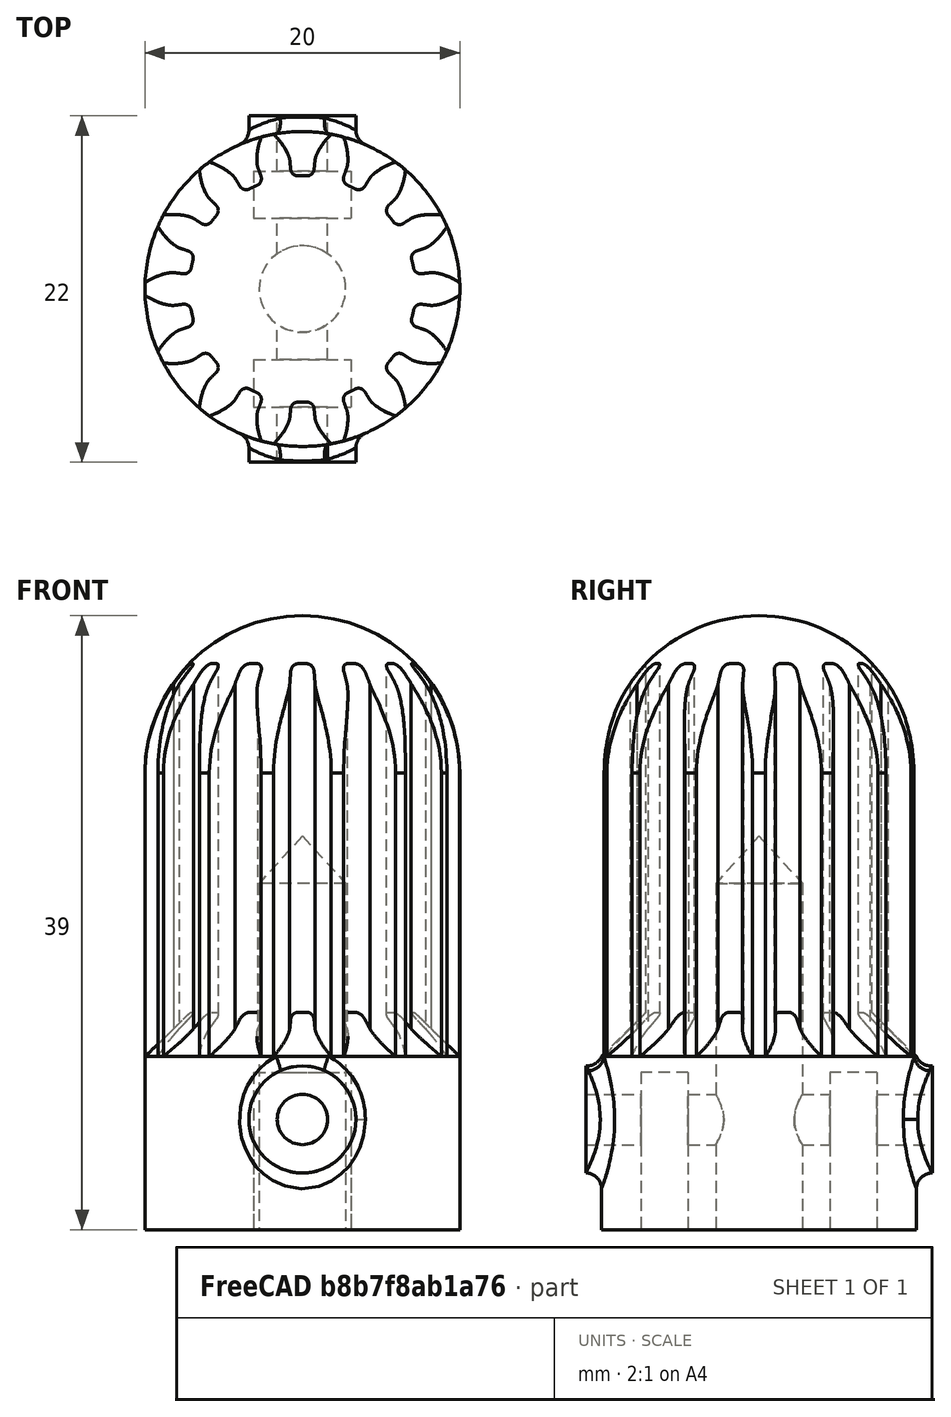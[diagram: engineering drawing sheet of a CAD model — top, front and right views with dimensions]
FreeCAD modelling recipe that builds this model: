
FCSTD DOCUMENT  (FreeCAD 0.14R3700 (Git))
Label: SmallGear
License: CC-BY 3.0
LicenseURL: http://creativecommons.org/licenses/by/3.0/
objects: Part::Cylinder×5, Part::Box×3, Part::Cut×3, Part::Sphere×2, Part::Cone×2, Part::MultiFuse×2, Part::Part2DObjectPython×1, PartDesign::Pad×1, Part::Fillet×1
note: 21 computed .brp shape members not serialized (recipe doc carries the construction recipe); baked Part::Feature solids carry a one-line shape summary decoded from their .brp

FEATURE [Part::Cylinder] Cylinder  label="CylinderBase"
  Angle = 360
  Height = 11
  Placement = pos=(0,0,28) rot=(0,0,1;0rad)
  Radius = 10
FEATURE [Part::Cylinder] Cylinder001  label="DeltaCylinderShaft"
  Angle = 360
  Height = 22
  Placement = pos=(0,0,17) rot=(0,0,1;0rad)
  Radius = 2.75
FEATURE [Part::Part2DObjectPython] InvoluteGear  # Draft 2D object (typed FeaturePython)
  Modules = 1.25
  NumberOfCurves = 0
  NumberOfTeeth = 14
  PressureAngle = 20
FEATURE [PartDesign::Pad] Pad
  Length = 28
  Length2 = 100
  Sketch = -> InvoluteGear
  Type = 0
FEATURE [Part::Box] Box  label="DeltaNutPocket1"
  Height = 10
  Length = 6.2
  Placement = pos=(-3.1,4.5,29) rot=(0,0,1;0rad)
  Width = 3
FEATURE [Part::Box] Box001  label="DeltaNutPocket2"
  Height = 10
  Length = 6.2
  Placement = pos=(-3.1,-7.5,29) rot=(0,0,1;0rad)
  Width = 3
FEATURE [Part::Cylinder] Cylinder002  label="DeltaCylinderM3"
  Angle = 360
  Height = 25
  Placement = pos=(0,13,32) rot=(1,0,0;1.5708rad)
  Radius = 1.6
FEATURE [Part::Sphere] Sphere  label="SphereTop"
  Angle1 = -90
  Angle2 = 90
  Angle3 = 360
  Placement = pos=(0,0,10) rot=(0,0,1;0rad)
  Radius = 10
FEATURE [Part::Box] Box002  label="DeltaCube"
  Height = 22
  Length = 44
  Placement = pos=(-22,-22,10) rot=(0,0,1;0rad)
  Width = 44
FEATURE [Part::Cone] Cone  label="ConeBase"
  Angle = 360
  Height = 5
  Placement = pos=(0,0,23) rot=(0,0,1;0rad)
  Radius1 = 5
  Radius2 = 10
FEATURE [Part::Sphere] Sphere001  label="SphereTopOutter"
  Angle1 = -90
  Angle2 = 90
  Angle3 = 360
  Placement = pos=(0,0,10) rot=(0,0,1;0rad)
  Radius = 20
FEATURE [Part::Cut] Cut
  Base = -> Sphere001
  Tool = -> Sphere
FEATURE [Part::Cut] Cut001  label="DeltaSphere"
  Base = -> Cut
  Tool = -> Box002
FEATURE [Part::Cone] Cone001  label="DeltaCylinderShaftTop"
  Angle = 360
  Height = 3
  Placement = pos=(0,0,14) rot=(0,0,1;0rad)
  Radius1 = 0
  Radius2 = 2.75
FEATURE [Part::Cylinder] Cylinder003  label="CylinderReenforcement1"
  Angle = 360
  Height = 3
  Placement = pos=(0,11,32) rot=(1,0,0;1.5708rad)
  Radius = 3.4
FEATURE [Part::Cylinder] Cylinder004  label="CylinderReenforcement2"
  Angle = 360
  Height = 3
  Placement = pos=(0,-8,32) rot=(1,0,0;1.5708rad)
  Radius = 3.4
FEATURE [Part::MultiFuse] Fusion
  Shapes = -> [Cone,Pad,Cylinder,Cylinder003,Cylinder004]
FEATURE [Part::MultiFuse] Fusion001  label="DeltaFusion"
  Shapes = -> [Cut001,Cone001,Cylinder002,Cylinder001,Box,Box001]
FEATURE [Part::Cut] Cut002
  Base = -> Fusion
  Tool = -> Fusion001
FEATURE [Part::Fillet] Fillet  label="SmallGear"
  Base = -> Cut002
  Edges = 2 edges r=1: [Edge4,Edge38]
  Placement = pos=(0,0,0) rot=(1,0,0;3.14159rad)
